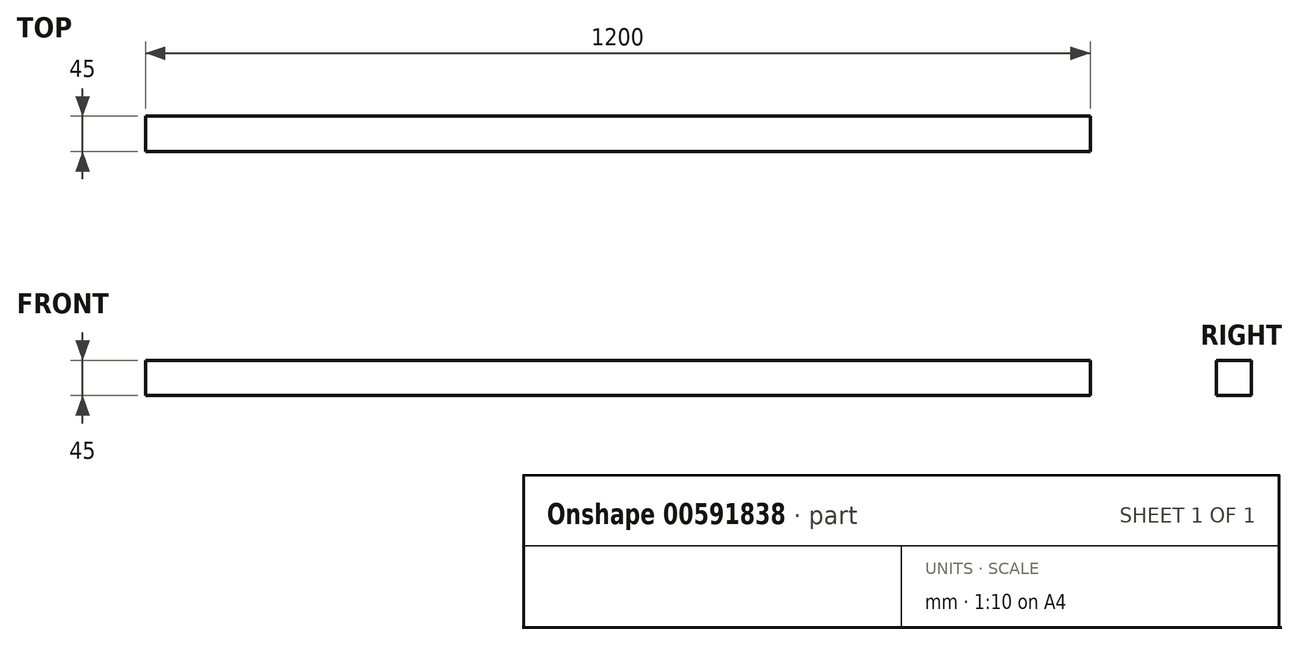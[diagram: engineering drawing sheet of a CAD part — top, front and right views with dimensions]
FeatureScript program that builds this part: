
annotation { "Feature Type Name" : "Feature", "Feature Type Description" : "" }
export const myFeature = defineFeature(function(context is Context, id is Id, definition is map)
    precondition{}
    {
        {
            var Q0;
            Q0=qCreatedBy(makeId("Right.planeOp"),FACE);
            var sketch = newSketch(context, id + "F0", { "sketchPlane" : qUnion([Q0])});
            skLineSegment(sketch, "E0.bottom", {"start": v(0, 0) * mm, "end": v(45, 0) * mm});
            skLineSegment(sketch, "E0.top", {"start": v(0, 45) * mm, "end": v(45, 45) * mm});
            skLineSegment(sketch, "E0.left", {"start": v(0, 0) * mm, "end": v(0, 45) * mm});
            skLineSegment(sketch, "E0.right", {"start": v(45, 0) * mm, "end": v(45, 45) * mm});
            skSolve(sketch);
        }
        {
            var Q0;
            Q0=makeQuery(id+"F0.imprint","IMPRINT",FACE,{"disambiguationData":[TD([[makeQuery(id+"F0.imprint","IMPRINT",EDGE,{"derivedFrom":sQuery(id+"F0.wireOp",EDGE,"E0.bottom")}),1.0]])]});
            extrude(context, id + "F1", {"entities" : qUnion([Q0]), "depth" : 1200 * mm, "offsetDistance" : 25 * mm});
        }
    });
